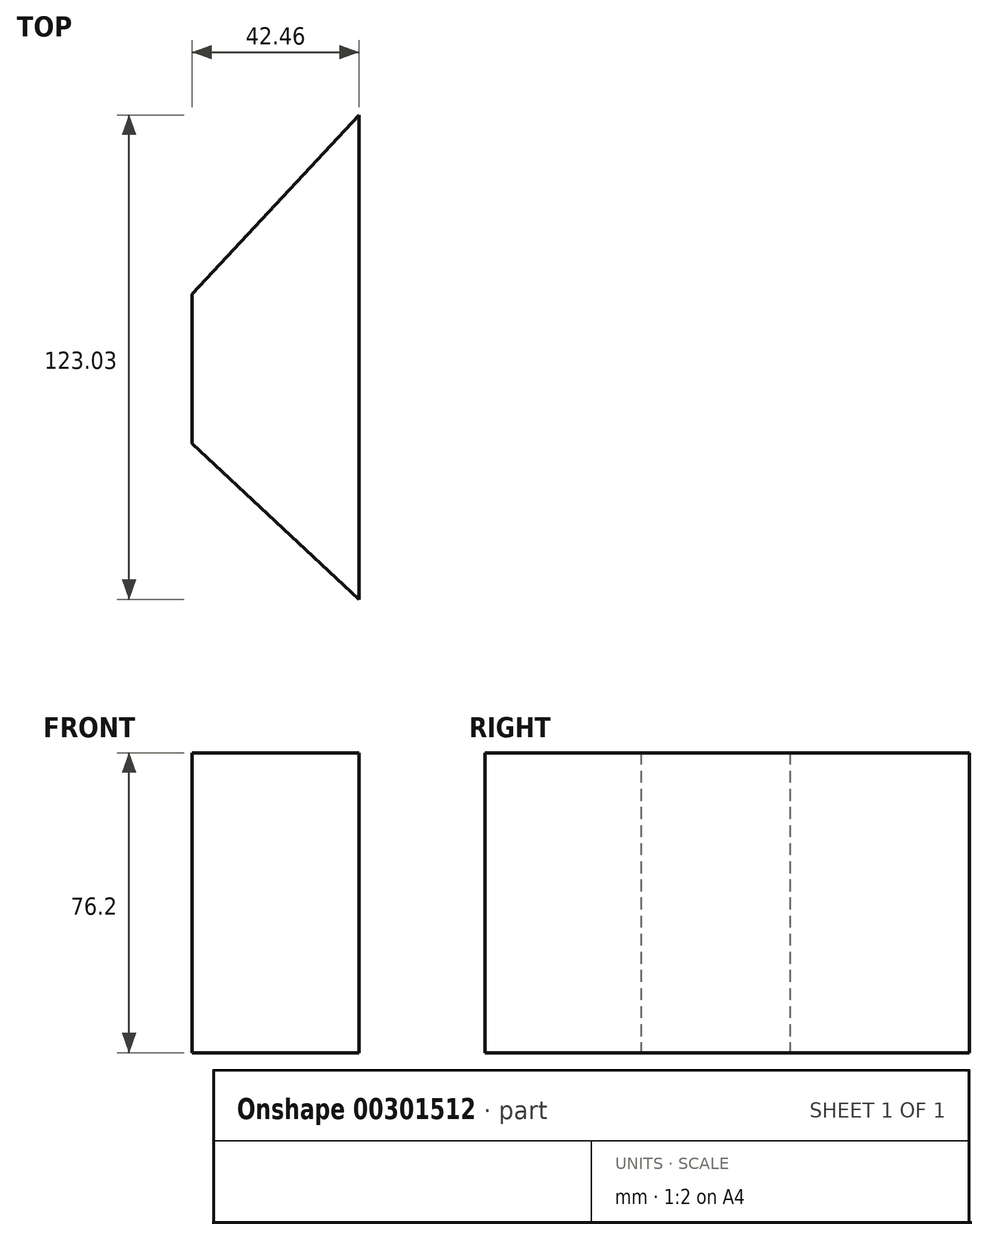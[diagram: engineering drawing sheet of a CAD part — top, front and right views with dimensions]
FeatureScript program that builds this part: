
annotation { "Feature Type Name" : "Feature", "Feature Type Description" : "" }
export const myFeature = defineFeature(function(context is Context, id is Id, definition is map)
    precondition{}
    {
        {
            var Q0;
            Q0=qCreatedBy(makeId("Top.planeOp"),FACE);
            var sketch = newSketch(context, id + "F0", { "sketchPlane" : qUnion([Q0])});
            skLineSegment(sketch, "E0", {"start": v(0, 0) * mm, "end": v(42.46, 45.55) * mm});
            skLineSegment(sketch, "E1", {"start": v(42.46, 45.55) * mm, "end": v(42.46, -77.48) * mm});
            skLineSegment(sketch, "E2", {"start": v(42.46, -77.48) * mm, "end": v(0, -37.93) * mm});
            skLineSegment(sketch, "E3", {"start": v(0, -37.93) * mm, "end": v(0, 0) * mm});
            skSolve(sketch);
        }
        {
            var Q0;
            Q0=makeQuery(id+"F0.imprint","IMPRINT",FACE,{"disambiguationData":[TD([[makeQuery(id+"F0.imprint","IMPRINT",EDGE,{"derivedFrom":sQuery(id+"F0.wireOp",EDGE,"E0")}),-1.0]])]});
            extrude(context, id + "F1", {"entities" : qUnion([Q0]), "depth" : 76.2 * mm});
        }
    });
